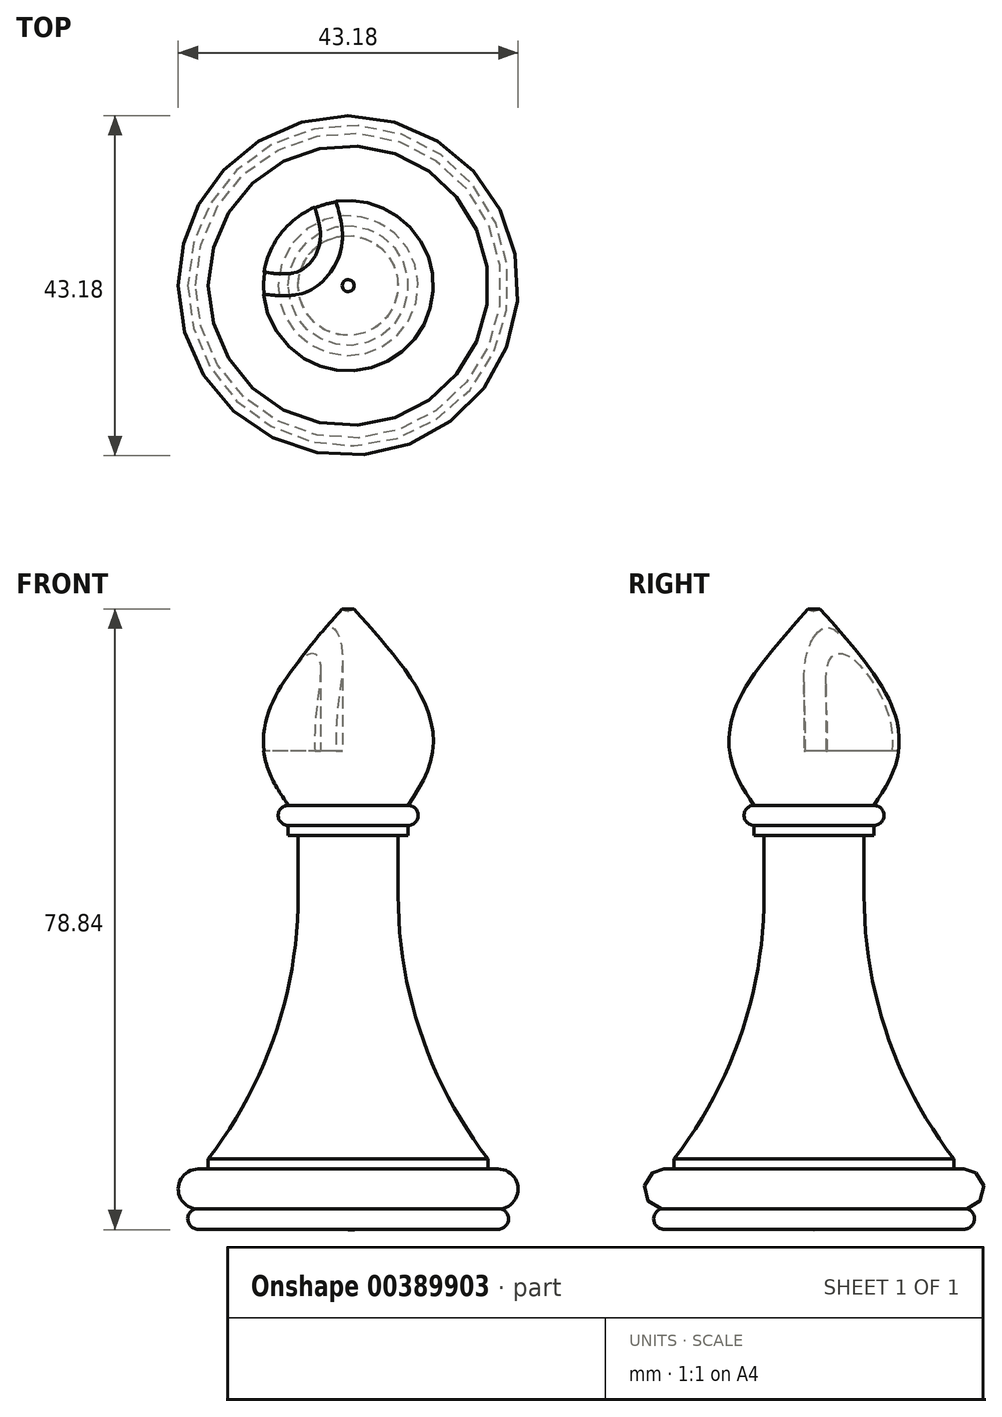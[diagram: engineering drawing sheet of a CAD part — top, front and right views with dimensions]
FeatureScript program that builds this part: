
annotation { "Feature Type Name" : "Feature", "Feature Type Description" : "" }
export const myFeature = defineFeature(function(context is Context, id is Id, definition is map)
    precondition{}
    {
        {
            var Q0;
            Q0=qCreatedBy(makeId("Front.planeOp"),FACE);
            var sketch = newSketch(context, id + "F0", { "sketchPlane" : qUnion([Q0])});
            skLineSegment(sketch, "E0", {"start": v(19.92, -0.03) * mm, "end": v(0.87, -0.08) * mm});
            skLineSegment(sketch, "E1", {"start": v(0.87, 0) * mm, "end": v(0.87, 81.28) * mm});
            skPoint(sketch, "E1.startSnap0", {"position": v(0.87, -0.08) * mm});
            skPoint(sketch, "E1.endSnap0", {"position": v(0.87, 5.08) * mm});
            skLineSegment(sketch, "E2", {"start": v(19.92, 2.54) * mm, "end": v(0.87, 2.54) * mm});
            skLineSegment(sketch, "E3", {"start": v(19.92, 7.62) * mm, "end": v(0.87, 7.62) * mm});
            skArc(sketch, "E4", {"start": v(19.92, 2.54) * mm, "mid": v(22.46, 5.08) * mm, "end": v(19.92, 7.62) * mm});
            skArc(sketch, "E5", {"start": v(19.92, -0.03) * mm, "mid": v(21.22, 1.11) * mm, "end": v(20.27, 2.56) * mm});
            skPoint(sketch, "E6.orphan", {"position": v(-18.18, -0.13) * mm});
            skLineSegment(sketch, "E7", {"start": v(18.65, 8.9) * mm, "end": v(18.65, 7.62) * mm});
            skPoint(sketch, "E8.startSnap0", {"position": v(10.4, 7.62) * mm});
            skLineSegment(sketch, "E9", {"start": v(0.87, 50) * mm, "end": v(8.49, 50) * mm});
            skPoint(sketch, "E10", {"position": v(7.22, 50) * mm});
            skLineSegment(sketch, "E11", {"start": v(7.22, 50) * mm, "end": v(7.22, 42.39) * mm});
            skArc(sketch, "E12", {"start": v(7.22, 42.39) * mm, "mid": v(10.15, 24.7) * mm, "end": v(18.65, 8.9) * mm});
            skLineSegment(sketch, "E13", {"start": v(8.49, 50) * mm, "end": v(8.49, 51.28) * mm});
            skLineSegment(sketch, "E14", {"start": v(8.49, 51.28) * mm, "end": v(0.87, 51.28) * mm});
            skLineSegment(sketch, "E15", {"start": v(8.49, 53.82) * mm, "end": v(0.87, 53.82) * mm});
            skArc(sketch, "E16", {"start": v(8.49, 51.28) * mm, "mid": v(9.76, 52.55) * mm, "end": v(8.49, 53.82) * mm});
            skPoint(sketch, "E8.start.orphan", {"position": v(10.4, 53.2) * mm});
            skLineSegment(sketch, "E17", {"start": v(1.64, 78.76) * mm, "end": v(0.87, 78.76) * mm});
            skFitSpline(sketch, "E18", {"points": [v(1.64, 78.76) * mm, v(10.78, 66.4) * mm, v(11.27, 59.12) * mm, v(8.49, 53.82) * mm], "startDerivative": vector(26.24, -29.45) * mm, "endDerivative": vector(-12.33, -18.64) * mm});
            skArc(sketch, "E19", {"start": v(1.64, 78.76) * mm, "mid": v(2.2, 80.3) * mm, "end": v(0.87, 81.28) * mm});
            skLineSegment(sketch, "E20", {"start": v(20.27, 2.56) * mm, "end": v(20.27, 2.56) * mm});
            skLineSegment(sketch, "E21", {"start": v(0.87, 0) * mm, "end": v(0.87, -0.08) * mm});
            skSolve(sketch);
        }
        {
            var Q0;
            Q0 = qSketchRegion(id + "F0", true);
            var Q1;
            Q1=sQuery(id+"F0.wireOp",EDGE,"E1");
            revolve(context, id + "F1", {"entities" : qUnion([Q0]), "axis" : qUnion([Q1]), "revolveType" : RevolveType.FULL});
        }
        {
            var Q0;
            Q0=qCreatedBy(makeId("Top.planeOp"),FACE);
            cPlane(context, id + "F2", {"entities" : qUnion([Q0]), "cplaneType" : CPlaneType.OFFSET, "offset" : 98.55 * mm, "width" : 152.4 * mm, "height" : 152.4 * mm});
        }
        {
            var Q0;
            Q0=qCreatedBy(id+"F2.planeOp",FACE);
            var sketch = newSketch(context, id + "F3", { "sketchPlane" : qUnion([Q0])});
            skFitSpline(sketch, "E22", {"points": [v(-0.89, 11.34) * mm, v(0, 4.75) * mm, v(-4.05, -0.64) * mm, v(-10.73, -0.98) * mm], "startDerivative": vector(6.07, -19.82) * mm, "endDerivative": vector(-21.16, 2.74) * mm});
            skFitSpline(sketch, "E23.0", {"points": [v(-3.56, 10.52) * mm, v(-3.3, 9.7) * mm, v(-2.96, 8.54) * mm, v(-2.7, 7.2) * mm, v(-2.64, 6.47) * mm, v(-2.65, 5.93) * mm, v(-2.69, 5.55) * mm, v(-2.76, 5.18) * mm, v(-2.87, 4.8) * mm, v(-3.02, 4.4) * mm, v(-3.28, 3.87) * mm, v(-3.68, 3.22) * mm, v(-4.17, 2.67) * mm, v(-4.57, 2.31) * mm, v(-4.88, 2.09) * mm, v(-5.17, 1.92) * mm, v(-5.45, 1.79) * mm, v(-5.76, 1.68) * mm, v(-6.22, 1.58) * mm, v(-6.91, 1.5) * mm, v(-8.26, 1.52) * mm, v(-9.49, 1.67) * mm, v(-10.37, 1.79) * mm]});
            skLineSegment(sketch, "E24", {"start": v(-10.37, 1.79) * mm, "end": v(-10.73, -0.98) * mm});
            skLineSegment(sketch, "E25", {"start": v(-3.56, 10.52) * mm, "end": v(-0.89, 11.34) * mm});
            skSolve(sketch);
        }
        {
            var Q0;
            Q0 = qSketchRegion(id + "F3", true);
            extrude(context, id + "F4", {"entities" : qUnion([Q0]), "operationType" : NewBodyOperationType.REMOVE, "oppositeDirection" : true, "depth" : 37.85 * mm});
        }
    });
